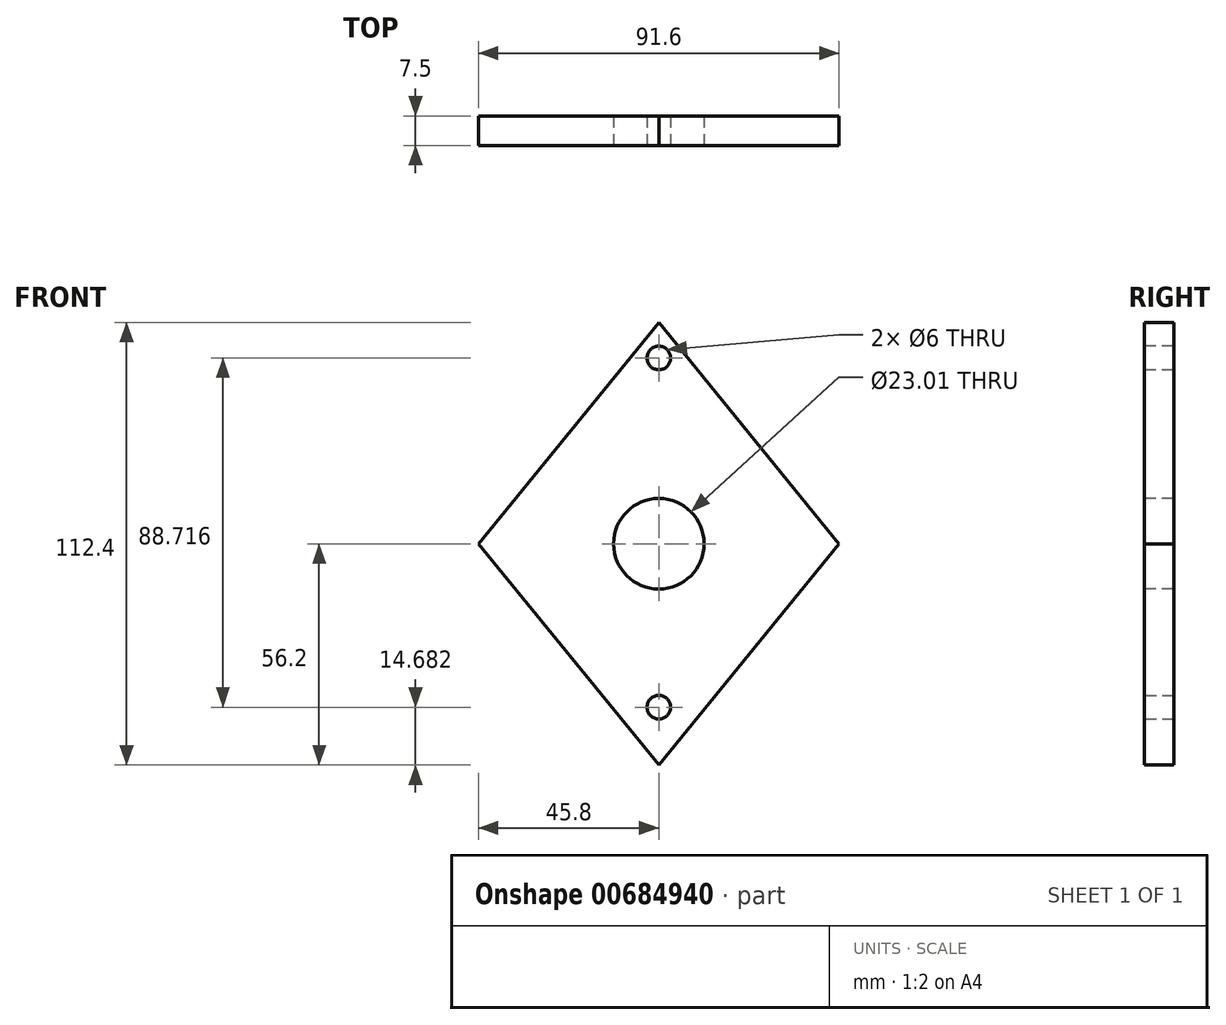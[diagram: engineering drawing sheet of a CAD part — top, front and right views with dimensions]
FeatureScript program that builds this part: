
annotation { "Feature Type Name" : "Feature", "Feature Type Description" : "" }
export const myFeature = defineFeature(function(context is Context, id is Id, definition is map)
    precondition{}
    {
        {
            var Q0;
            Q0=qCreatedBy(makeId("Front.planeOp"),FACE);
            var sketch = newSketch(context, id + "F0", { "sketchPlane" : qUnion([Q0])});
            skLineSegment(sketch, "E0", {"start": v(0, 56.2) * mm, "end": v(-45.8, 0) * mm});
            skLineSegment(sketch, "E1", {"start": v(-45.8, 0) * mm, "end": v(0, -56.2) * mm});
            skLineSegment(sketch, "E2", {"start": v(0, -56.2) * mm, "end": v(45.8, 0) * mm});
            skLineSegment(sketch, "E3", {"start": v(45.8, 0) * mm, "end": v(0, 56.2) * mm});
            skSolve(sketch);
        }
        {
            var Q0;
            Q0=makeQuery(id+"F0.imprint","IMPRINT",FACE,{"disambiguationData":[TD([[makeQuery(id+"F0.imprint","IMPRINT",EDGE,{"derivedFrom":sQuery(id+"F0.wireOp",EDGE,"E0")}),1.0]])]});
            extrude(context, id + "F1", {"entities" : qUnion([Q0]), "depth" : 7.5 * mm, "offsetDistance" : 25 * mm});
        }
        {
            var Q0;
            Q0=makeQuery(id+"F1.opExtrude","CAP_FACE",FACE,{"disambiguationData":[OSD([sQuery(id+"F0.wireOp",EDGE,"E0"),sQuery(id+"F0.wireOp",EDGE,"E1"),sQuery(id+"F0.wireOp",EDGE,"E2"),sQuery(id+"F0.wireOp",EDGE,"E3")])],"isStart":false});
            var sketch = newSketch(context, id + "F2", { "sketchPlane" : qUnion([Q0])});
            skCircle(sketch, "E4", {"center": v(0, 0) * mm, "radius": 11.5 * mm});
            skSolve(sketch);
        }
        {
            var Q0;
            Q0 = qSketchRegion(id + "F2", true);
            extrude(context, id + "F3", {"entities" : qUnion([Q0]), "operationType" : NewBodyOperationType.REMOVE, "oppositeDirection" : true, "depth" : 25 * mm, "offsetDistance" : 25 * mm});
        }
        {
            var Q0;
            Q0=makeQuery(id+"F1.opExtrude","CAP_FACE",FACE,{"disambiguationData":[OSD([sQuery(id+"F0.wireOp",EDGE,"E0"),sQuery(id+"F0.wireOp",EDGE,"E1"),sQuery(id+"F0.wireOp",EDGE,"E2"),sQuery(id+"F0.wireOp",EDGE,"E3")])],"isStart":false});
            var sketch = newSketch(context, id + "F4", { "sketchPlane" : qUnion([Q0])});
            skCircle(sketch, "E5", {"center": v(0, 47.2) * mm, "radius": 3 * mm});
            skSolve(sketch);
        }
        {
            var Q0;
            Q0=makeQuery(id+"F4.imprint","IMPRINT",FACE,{"disambiguationData":[TD([[makeQuery(id+"F4.imprint","IMPRINT",EDGE,{"derivedFrom":sQuery(id+"F4.wireOp",EDGE,"E5")}),1.0]])]});
            extrude(context, id + "F5", {"entities" : qUnion([Q0]), "operationType" : NewBodyOperationType.REMOVE, "oppositeDirection" : true, "depth" : 25 * mm, "offsetDistance" : 25 * mm});
        }
        {
            var Q0;
            Q0=makeQuery(id+"F1.opExtrude","CAP_FACE",FACE,{"disambiguationData":[OSD([sQuery(id+"F0.wireOp",EDGE,"E0"),sQuery(id+"F0.wireOp",EDGE,"E1"),sQuery(id+"F0.wireOp",EDGE,"E2"),sQuery(id+"F0.wireOp",EDGE,"E3")])],"isStart":true});
            var sketch = newSketch(context, id + "F6", { "sketchPlane" : qUnion([Q0])});
            skCircle(sketch, "E6", {"center": v(0, -41.52) * mm, "radius": 3 * mm});
            skSolve(sketch);
        }
        {
            var Q0;
            Q0 = qSketchRegion(id + "F6", true);
            extrude(context, id + "F7", {"entities" : qUnion([Q0]), "operationType" : NewBodyOperationType.REMOVE, "oppositeDirection" : true, "depth" : 25 * mm, "offsetDistance" : 25 * mm});
        }
    });
